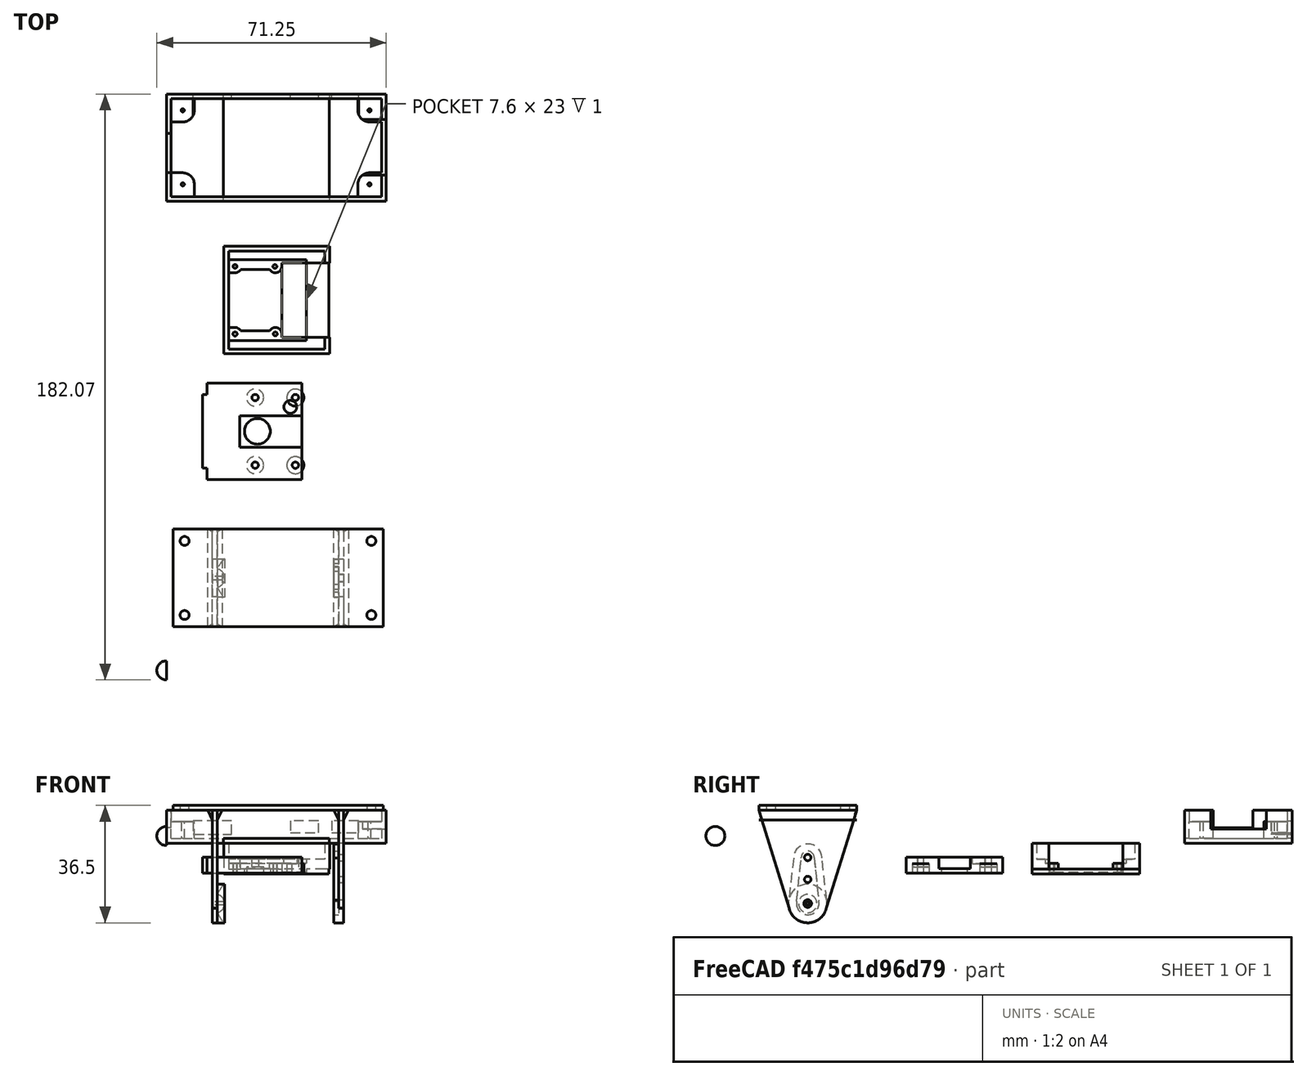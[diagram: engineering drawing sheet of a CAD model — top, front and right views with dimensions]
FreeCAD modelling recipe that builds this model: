
FCSTD DOCUMENT  (FreeCAD 0.18.3R)
Label: Vertical.Turning.PI.Box
License: All rights reserved
LicenseURL: http://en.wikipedia.org/wiki/All_rights_reserved
objects: Part::Part2DObjectPython×108, Part::Extrusion×94, Part::Cut×46, Part::MultiFuse×22, Part::FeaturePython×6, Part::Sphere×2, App::DocumentObjectGroup×2
note: 278 computed .brp shape members not serialized (recipe doc carries the construction recipe); baked Part::Feature solids carry a one-line shape summary decoded from their .brp

FEATURE [Part::Part2DObjectPython] Rectangle  # Draft 2D object (typed FeaturePython)
  ChamferSize = 0
  Columns = 1
  FilletRadius = 0
  Height = 33.4
  Length = 68.3
  MakeFace = true
  Placement = pos=(0,0,0) rot=(1,0,0;3.14159rad)
  Rows = 1
FEATURE [Part::Part2DObjectPython] Rectangle001  # Draft 2D object (typed FeaturePython)
  ChamferSize = 0
  Columns = 1
  FilletRadius = 0
  Height = 30.4
  Length = 65.3
  MakeFace = true
  Placement = pos=(1.5,-1.5,0) rot=(1,0,0;3.14159rad)
  Rows = 1
FEATURE [Part::Part2DObjectPython] Circle004  # Draft 2D object (typed FeaturePython)
  FirstAngle = 0
  LastAngle = 0
  MakeFace = true
  Placement = pos=(5.1,-5.1,-8.3) rot=(0,0,-1;1.5708rad)
  Radius = 3.6
FEATURE [Part::Part2DObjectPython] Circle006  # Draft 2D object (typed FeaturePython)
  FirstAngle = 0
  LastAngle = 0
  MakeFace = true
  Placement = pos=(63.1,-5.1,-8.3) rot=(0,0,1;0rad)
  Radius = 3.6
FEATURE [Part::Part2DObjectPython] Rectangle006  # Draft 2D object (typed FeaturePython)
  ChamferSize = 0
  Columns = 1
  FilletRadius = 0
  Height = 4.1
  Length = 11.9
  MakeFace = true
  Placement = pos=(8.375,-1.5,-7) rot=(1,0,0;1.5708rad)
  Rows = 1
FEATURE [Part::Part2DObjectPython] Rectangle007  # Draft 2D object (typed FeaturePython)
  ChamferSize = 0
  Columns = 1
  FilletRadius = 0
  Height = 3.7
  Length = 8.7
  MakeFace = true
  Placement = pos=(38.55,-1.5,-6.5) rot=(1,0,0;1.5708rad)
  Rows = 1
FEATURE [Part::Part2DObjectPython] Rectangle008  # Draft 2D object (typed FeaturePython)
  ChamferSize = 0
  Columns = 1
  FilletRadius = 0
  Height = 3.7
  Length = 8.4
  MakeFace = true
  Placement = pos=(51.35,-1.5,-6.5) rot=(1,0,0;1.5708rad)
  Rows = 1
  Support = -> [Rectangle007]
FEATURE [Part::Extrusion] Extrude020
  Base = -> Circle006
  Dir = (0,0,1)
  DirMode = 2
  FaceMakerClass = Part::FaceMakerBullseye
  LengthFwd = 5.3
  LengthRev = 0
  Solid = false
  Symmetric = false
FEATURE [Part::Extrusion] Extrude021
  Base = -> Circle004
  Dir = (0,0,1)
  DirMode = 2
  FaceMakerClass = Part::FaceMakerBullseye
  LengthFwd = 5.3
  LengthRev = 0
  Solid = false
  Symmetric = false
FEATURE [Part::Part2DObjectPython] Rectangle013  # Draft 2D object (typed FeaturePython)
  ChamferSize = 0
  Columns = 1
  FilletRadius = 0
  Height = 7.2
  Length = 3.6
  MakeFace = true
  Placement = pos=(1.5,-8.7,-8.3) rot=(0,0,1;0rad)
  Rows = 1
  Support = -> [Rectangle]
FEATURE [Part::Part2DObjectPython] Rectangle014  # Draft 2D object (typed FeaturePython)
  ChamferSize = 0
  Columns = 1
  FilletRadius = 0
  Height = 3.6
  Length = 7.2
  MakeFace = true
  Placement = pos=(1.5,-5.1,-8.3) rot=(0,0,1;0rad)
  Rows = 1
FEATURE [Part::Part2DObjectPython] Circle008  # Draft 2D object (typed FeaturePython)
  FirstAngle = 0
  LastAngle = 0
  MakeFace = true
  Placement = pos=(63.1,-5.1,-8.3) rot=(0,0,1;0rad)
  Radius = 0.5
FEATURE [Part::Extrusion] Extrude027
  Base = -> Circle008
  Dir = (0,0,1)
  DirMode = 2
  FaceMakerClass = Part::FaceMakerBullseye
  LengthFwd = 5.3
  LengthRev = 0
  Solid = false
  Symmetric = false
FEATURE [Part::Extrusion] Extrude028
  Base = -> Rectangle013
  Dir = (0,0,1)
  DirMode = 2
  FaceMakerClass = Part::FaceMakerBullseye
  LengthFwd = 5.3
  LengthRev = 0
  Solid = false
  Symmetric = false
FEATURE [Part::Extrusion] Extrude029
  Base = -> Rectangle014
  Dir = (0,0,1)
  DirMode = 2
  FaceMakerClass = Part::FaceMakerBullseye
  LengthFwd = 5.3
  LengthRev = 0
  Solid = false
  Symmetric = false
FEATURE [Part::MultiFuse] Fusion002
  Shapes = -> [Extrude028,Extrude029,Extrude021]
FEATURE [Part::Part2DObjectPython] Circle009  # Draft 2D object (typed FeaturePython)
  FirstAngle = 0
  LastAngle = 0
  MakeFace = true
  Placement = pos=(5.1,-5.1,-8.3) rot=(0,0,1;0rad)
  Radius = 0.5
FEATURE [Part::Extrusion] Extrude030
  Base = -> Circle009
  Dir = (0,0,1)
  DirMode = 2
  FaceMakerClass = Part::FaceMakerBullseye
  LengthFwd = 5.3
  LengthRev = 0
  Solid = false
  Symmetric = false
FEATURE [Part::Cut] Cut002
  Base = -> Fusion002
  Tool = -> Extrude030
FEATURE [Part::Part2DObjectPython] Circle010  # Draft 2D object (typed FeaturePython)
  FirstAngle = 0
  LastAngle = 0
  MakeFace = true
  Placement = pos=(5.1,-28.1,-8.3) rot=(1,0,0;3.14159rad)
  Radius = 0.5
FEATURE [Part::Extrusion] Extrude033
  Base = -> Circle010
  Dir = (0,0,-1)
  DirMode = 2
  FaceMakerClass = Part::FaceMakerBullseye
  LengthFwd = -5.3
  LengthRev = 0
  Solid = false
  Symmetric = false
FEATURE [Part::Part2DObjectPython] Circle011  # Draft 2D object (typed FeaturePython)
  FirstAngle = 0
  LastAngle = 0
  MakeFace = true
  Placement = pos=(5.1,-28.1,-8.3) rot=(1,0,0;3.14159rad)
  Radius = 3.6
FEATURE [Part::Part2DObjectPython] Rectangle019  # Draft 2D object (typed FeaturePython)
  ChamferSize = 0
  Columns = 1
  FilletRadius = 0
  Height = 3.8
  Length = 7.2
  MakeFace = true
  Placement = pos=(1.5,-31.9,-8.3) rot=(0,0,1;0rad)
  Rows = 1
FEATURE [Part::Part2DObjectPython] Rectangle020  # Draft 2D object (typed FeaturePython)
  ChamferSize = 0
  Columns = 1
  FilletRadius = 0
  Height = 7.4
  Length = 3.6
  MakeFace = true
  Placement = pos=(1.5,-31.9,-8.3) rot=(0,0,1;0rad)
  Rows = 1
FEATURE [Part::Extrusion] Extrude
  Base = -> Circle011
  Dir = (0,0,-1)
  DirMode = 2
  FaceMakerClass = Part::FaceMakerBullseye
  LengthFwd = -5.3
  LengthRev = 0
  Solid = false
  Symmetric = false
FEATURE [Part::Extrusion] Extrude034
  Base = -> Rectangle019
  Dir = (0,0,1)
  DirMode = 2
  FaceMakerClass = Part::FaceMakerBullseye
  LengthFwd = 5.3
  LengthRev = 0
  Solid = false
  Symmetric = false
FEATURE [Part::Extrusion] Extrude035
  Base = -> Rectangle020
  Dir = (0,0,1)
  DirMode = 2
  FaceMakerClass = Part::FaceMakerBullseye
  LengthFwd = 5.3
  LengthRev = 0
  Solid = false
  Symmetric = false
FEATURE [Part::MultiFuse] Fusion003
  Shapes = -> [Extrude034,Extrude035,Extrude]
FEATURE [Part::Cut] Cut003
  Base = -> Fusion003
  Tool = -> Extrude033
FEATURE [Part::Extrusion] Extrude036
  Base = -> Rectangle001
  Dir = (0,0,-1)
  DirMode = 2
  FaceMakerClass = Part::FaceMakerBullseye
  LengthFwd = 8.3
  LengthRev = 0
  Solid = false
  Symmetric = false
FEATURE [Part::Extrusion] Extrude037
  Base = -> Rectangle
  Dir = (0,0,-1)
  DirMode = 2
  FaceMakerClass = Part::FaceMakerBullseye
  LengthFwd = 9.8
  LengthRev = 0
  Solid = false
  Symmetric = false
FEATURE [Part::Part2DObjectPython] Circle012  # Draft 2D object (typed FeaturePython)
  FirstAngle = 0
  LastAngle = 0
  MakeFace = true
  Placement = pos=(63.1,-28.1,-3) rot=(0,0,1;0rad)
  Radius = 3.6
FEATURE [Part::Part2DObjectPython] Circle013  # Draft 2D object (typed FeaturePython)
  FirstAngle = 0
  LastAngle = 0
  MakeFace = true
  Placement = pos=(63.1,-28.1,-3) rot=(0,0,1;0rad)
  Radius = 0.5
FEATURE [Part::Part2DObjectPython] Rectangle021  # Draft 2D object (typed FeaturePython)
  ChamferSize = 0
  Columns = 1
  FilletRadius = 0
  Height = 7.4
  Length = 3.7
  MakeFace = true
  Placement = pos=(63.1,-31.9,-3) rot=(0,0,1;0rad)
  Rows = 1
FEATURE [Part::Part2DObjectPython] Rectangle022  # Draft 2D object (typed FeaturePython)
  ChamferSize = 0
  Columns = 1
  FilletRadius = 0
  Height = 3.8
  Length = 7.3
  MakeFace = true
  Placement = pos=(59.5,-31.9,-3) rot=(0,0,1;0rad)
  Rows = 1
FEATURE [Part::Extrusion] Extrude038
  Base = -> Rectangle021
  Dir = (0,0,1)
  DirMode = 2
  FaceMakerClass = Part::FaceMakerBullseye
  LengthFwd = -5.3
  LengthRev = 0
  Solid = false
  Symmetric = false
FEATURE [Part::Extrusion] Extrude039
  Base = -> Rectangle022
  Dir = (0,0,1)
  DirMode = 2
  FaceMakerClass = Part::FaceMakerBullseye
  LengthFwd = -5.3
  LengthRev = 0
  Solid = false
  Symmetric = false
FEATURE [Part::Extrusion] Extrude040
  Base = -> Circle012
  Dir = (0,0,1)
  DirMode = 2
  FaceMakerClass = Part::FaceMakerBullseye
  LengthFwd = -5.3
  LengthRev = 0
  Solid = false
  Symmetric = false
FEATURE [Part::Extrusion] Extrude041
  Base = -> Circle013
  Dir = (0,0,1)
  DirMode = 2
  FaceMakerClass = Part::FaceMakerBullseye
  LengthFwd = -5.3
  LengthRev = 0
  Solid = false
  Symmetric = false
FEATURE [Part::MultiFuse] Fusion
  Shapes = -> [Extrude038,Extrude039,Extrude040]
FEATURE [Part::Cut] Cut
  Base = -> Fusion
  Tool = -> Extrude041
FEATURE [Part::Part2DObjectPython] Rectangle024  # Draft 2D object (typed FeaturePython)
  ChamferSize = 0
  Columns = 1
  FilletRadius = 0
  Height = 3.6
  Length = 7.3
  MakeFace = true
  Placement = pos=(59.5,-5.1,-3) rot=(0,0,1;0rad)
  Rows = 1
FEATURE [Part::Part2DObjectPython] Rectangle025  # Draft 2D object (typed FeaturePython)
  ChamferSize = 0
  Columns = 1
  FilletRadius = 0
  Height = 7.19976
  Length = 3.7019
  MakeFace = true
  Placement = pos=(63.1,-8.7,-3) rot=(0,0,1;0rad)
  Rows = 1
FEATURE [Part::Extrusion] Extrude042
  Base = -> Rectangle025
  Dir = (0,0,1)
  DirMode = 2
  FaceMakerClass = Part::FaceMakerBullseye
  LengthFwd = -5.3
  LengthRev = 0
  Solid = false
  Symmetric = false
FEATURE [Part::Extrusion] Extrude043
  Base = -> Rectangle024
  Dir = (0,0,1)
  DirMode = 2
  FaceMakerClass = Part::FaceMakerBullseye
  LengthFwd = -5.3
  LengthRev = 0
  Solid = false
  Symmetric = false
FEATURE [Part::MultiFuse] Fusion004
  Shapes = -> [Extrude043,Extrude042,Extrude020]
FEATURE [Part::Cut] Cut005
  Base = -> Fusion004
  Tool = -> Extrude027
FEATURE [Part::Extrusion] Extrude046
  Base = -> Rectangle006
  Dir = (0,-1,2e-16)
  DirMode = 2
  FaceMakerClass = Part::FaceMakerBullseye
  LengthFwd = 7
  LengthRev = 0
  Solid = false
  Symmetric = false
FEATURE [Part::Cut] Cut008
  Base = -> Cut002
  Tool = -> Extrude046
FEATURE [Part::Part2DObjectPython] Rectangle028  # Draft 2D object (typed FeaturePython)
  ChamferSize = 0
  Columns = 1
  FilletRadius = 0
  Height = 4.2
  Length = 11.9
  MakeFace = true
  Placement = pos=(8.375,-1.5,-7) rot=(1,0,0;1.5708rad)
  Rows = 1
FEATURE [Part::Part2DObjectPython] Rectangle029  # Draft 2D object (typed FeaturePython)
  ChamferSize = 0
  Columns = 1
  FilletRadius = 0
  Height = 3.6
  Length = 8.4
  MakeFace = true
  Placement = pos=(51.35,-1.5,-6.5) rot=(1,0,0;1.5708rad)
  Rows = 1
FEATURE [Part::Extrusion] Extrude050
  Base = -> Rectangle029
  Dir = (0,-1,2e-16)
  DirMode = 2
  FaceMakerClass = Part::FaceMakerBullseye
  LengthFwd = 7
  LengthRev = 0
  Placement = pos=(7.1e-15,-9e-16,0) rot=(0,0,1;0rad)
  Solid = false
  Symmetric = false
FEATURE [Part::Part2DObjectPython] Circle018  # Draft 2D object (typed FeaturePython)
  FirstAngle = 0
  LastAngle = 0
  MakeFace = true
  Placement = pos=(80.1343,-53.566,-3.6) rot=(0,0,1;0rad)
  Radius = 2
FEATURE [Part::Part2DObjectPython] Circle019  # Draft 2D object (typed FeaturePython)
  FirstAngle = 0
  LastAngle = 0
  MakeFace = true
  Placement = pos=(80.1343,-74.566,-3.6) rot=(0,0,1;0rad)
  Radius = 2
FEATURE [Part::Part2DObjectPython] Circle020  # Draft 2D object (typed FeaturePython)
  FirstAngle = 0
  LastAngle = 0
  MakeFace = true
  Placement = pos=(67.6343,-74.566,-3.6) rot=(0,0,1;0rad)
  Radius = 2
FEATURE [Part::Part2DObjectPython] Circle021  # Draft 2D object (typed FeaturePython)
  FirstAngle = 0
  LastAngle = 0
  MakeFace = true
  Placement = pos=(67.6343,-53.566,-3.6) rot=(0,0,1;0rad)
  Radius = 2
FEATURE [Part::Part2DObjectPython] Rectangle043  # Draft 2D object (typed FeaturePython)
  ChamferSize = 0
  Columns = 1
  FilletRadius = 0
  Height = 30
  Length = 29.4
  MakeFace = true
  Placement = pos=(12.6799,-119.849,-14.1) rot=(0,0,1;0rad)
  Rows = 1
FEATURE [Part::Part2DObjectPython] Rectangle044  # Draft 2D object (typed FeaturePython)
  ChamferSize = 0
  Columns = 1
  FilletRadius = 0
  Height = 22.8
  Length = 1.5
  MakeFace = true
  Placement = pos=(11.1799,-116.249,-14.1) rot=(0,0,1;0rad)
  Rows = 1
FEATURE [Part::Part2DObjectPython] Rectangle045  # Draft 2D object (typed FeaturePython)
  ChamferSize = 0
  Columns = 1
  FilletRadius = 0
  Height = 9.8
  Length = 19.3
  MakeFace = true
  Placement = pos=(22.7799,-109.749,-14.1) rot=(0,0,1;0rad)
  Rows = 1
FEATURE [Part::Part2DObjectPython] Circle022  # Draft 2D object (typed FeaturePython)
  FirstAngle = 0
  LastAngle = 0
  MakeFace = true
  Placement = pos=(28.2799,-104.849,-14.1) rot=(0,0,1;0rad)
  Radius = 4
FEATURE [Part::MultiFuse] Fusion013
  Shapes = -> [Cut005,Cut]
FEATURE [Part::Part2DObjectPython] Circle  # Draft 2D object (typed FeaturePython)
  FirstAngle = 0
  LastAngle = 0
  MakeFace = true
  Placement = pos=(27.5799,-94.3491,-14.1) rot=(0,0,1;0rad)
  Radius = 1
FEATURE [Part::Part2DObjectPython] Circle023  # Draft 2D object (typed FeaturePython)
  FirstAngle = 0
  LastAngle = 0
  MakeFace = true
  Placement = pos=(40.0799,-94.3491,-14.1) rot=(0,0,1;0rad)
  Radius = 1
FEATURE [Part::Part2DObjectPython] Circle024  # Draft 2D object (typed FeaturePython)
  FirstAngle = 0
  LastAngle = 0
  MakeFace = true
  Placement = pos=(40.0799,-115.349,-14.1) rot=(0,0,1;0rad)
  Radius = 1
FEATURE [Part::Part2DObjectPython] Circle025  # Draft 2D object (typed FeaturePython)
  FirstAngle = 0
  LastAngle = 0
  MakeFace = true
  Placement = pos=(27.5799,-115.349,-14.1) rot=(0,0,1;0rad)
  Radius = 1
FEATURE [Part::Extrusion] Extrude083
  Base = -> Rectangle043
  Dir = (0,0,1)
  DirMode = 2
  FaceMakerClass = Part::FaceMakerBullseye
  LengthFwd = -5
  LengthRev = 0
  Solid = false
  Symmetric = false
FEATURE [Part::Extrusion] Extrude085
  Base = -> Rectangle045
  Dir = (0,0,1)
  DirMode = 2
  FaceMakerClass = Part::FaceMakerBullseye
  LengthFwd = -3.5
  LengthRev = 0
  Solid = false
  Symmetric = false
FEATURE [Part::Extrusion] Extrude086
  Base = -> Circle
  Dir = (0,0,1)
  DirMode = 2
  FaceMakerClass = Part::FaceMakerBullseye
  LengthFwd = -5
  LengthRev = 0
  Solid = false
  Symmetric = false
FEATURE [Part::Extrusion] Extrude087
  Base = -> Circle023
  Dir = (0,0,1)
  DirMode = 2
  FaceMakerClass = Part::FaceMakerBullseye
  LengthFwd = -5
  LengthRev = 0
  Solid = false
  Symmetric = false
FEATURE [Part::Extrusion] Extrude088
  Base = -> Circle025
  Dir = (0,0,1)
  DirMode = 2
  FaceMakerClass = Part::FaceMakerBullseye
  LengthFwd = -5
  LengthRev = 0
  Solid = false
  Symmetric = false
FEATURE [Part::Extrusion] Extrude089
  Base = -> Circle024
  Dir = (0,0,1)
  DirMode = 2
  FaceMakerClass = Part::FaceMakerBullseye
  LengthFwd = -5
  LengthRev = 0
  Solid = false
  Symmetric = false
FEATURE [Part::Cut] Cut027
  Base = -> Extrude083
  Tool = -> Extrude085
FEATURE [Part::Extrusion] Extrude095
  Base = -> Rectangle044
  Dir = (0,0,1)
  DirMode = 2
  FaceMakerClass = Part::FaceMakerBullseye
  LengthFwd = -5
  LengthRev = 0
  Solid = false
  Symmetric = false
FEATURE [Part::Part2DObjectPython] Rectangle048  # Draft 2D object (typed FeaturePython)
  ChamferSize = 0
  Columns = 1
  FilletRadius = 0
  Height = 4.99807
  Length = 12.3
  MakeFace = true
  Placement = pos=(1.5,-24.5,-4.99807) rot=(0.57735,0.57735,0.57735;2.0944rad)
  Rows = 1
FEATURE [Part::Extrusion] Extrude096
  Base = -> Rectangle048
  Dir = (1,0,0)
  DirMode = 2
  FaceMakerClass = Part::FaceMakerBullseye
  LengthFwd = -1.5
  LengthRev = 0
  Solid = false
  Symmetric = false
FEATURE [Part::Part2DObjectPython] Circle030  # Draft 2D object (typed FeaturePython)
  FirstAngle = 0
  LastAngle = 0
  MakeFace = true
  Placement = pos=(27.5799,-94.3491,-19.1) rot=(0,0,1;0rad)
  Radius = 2.65
FEATURE [Part::Part2DObjectPython] Circle031  # Draft 2D object (typed FeaturePython)
  FirstAngle = 0
  LastAngle = 0
  MakeFace = true
  Placement = pos=(27.5799,-115.349,-19.1) rot=(0,0,1;0rad)
  Radius = 2.65
FEATURE [Part::Part2DObjectPython] Circle032  # Draft 2D object (typed FeaturePython)
  FirstAngle = 0
  LastAngle = 0
  MakeFace = true
  Placement = pos=(40.0799,-115.349,-19.1) rot=(0,0,1;0rad)
  Radius = 2.65
FEATURE [Part::Part2DObjectPython] Circle033  # Draft 2D object (typed FeaturePython)
  FirstAngle = 0
  LastAngle = 0
  MakeFace = true
  Placement = pos=(40.0799,-94.3491,-19.1) rot=(0,0,1;0rad)
  Radius = 2.65
FEATURE [Part::Extrusion] Extrude104
  Base = -> Circle032
  Dir = (0,0,1)
  DirMode = 2
  FaceMakerClass = Part::FaceMakerBullseye
  LengthFwd = 3
  LengthRev = 0
  Solid = false
  Symmetric = false
FEATURE [Part::Extrusion] Extrude105
  Base = -> Circle033
  Dir = (0,0,1)
  DirMode = 2
  FaceMakerClass = Part::FaceMakerBullseye
  LengthFwd = 3
  LengthRev = 0
  Solid = false
  Symmetric = false
FEATURE [Part::Part2DObjectPython] Rectangle049  # Draft 2D object (typed FeaturePython)
  ChamferSize = 0
  Columns = 1
  FilletRadius = 0
  Height = 33.4
  Length = 32.95
  MakeFace = true
  Placement = pos=(17.675,-33.4,-10.8) rot=(0,0,1;0rad)
  Rows = 1
FEATURE [Part::Part2DObjectPython] Rectangle060  # Draft 2D object (typed FeaturePython)
  ChamferSize = 0
  Columns = 1
  FilletRadius = 0
  Height = 23
  Length = 14.4
  MakeFace = true
  Placement = pos=(52.2343,-52.566,-9.8) rot=(1,0,0;3.14159rad)
  Rows = 1
FEATURE [Part::Part2DObjectPython] Rectangle053  # Draft 2D object (typed FeaturePython)
  ChamferSize = 0
  Columns = 1
  FilletRadius = 0
  Height = 33.4
  Length = 32.9
  MakeFace = true
  Placement = pos=(50.7343,-47.366,-9.8) rot=(1,0,0;3.14159rad)
  Rows = 1
FEATURE [Part::Part2DObjectPython] Rectangle061  # Draft 2D object (typed FeaturePython)
  ChamferSize = 0
  Columns = 1
  FilletRadius = 0
  Height = 25.1
  Length = 24.1
  MakeFace = true
  Placement = pos=(58.0343,-51.516,-9.8) rot=(1,0,0;3.14159rad)
  Rows = 1
FEATURE [Part::Part2DObjectPython] Rectangle059  # Draft 2D object (typed FeaturePython)
  ChamferSize = 0
  Columns = 1
  FilletRadius = 0
  Height = 19
  Length = 15.5
  MakeFace = true
  Placement = pos=(66.6343,-54.566,-9.8) rot=(1,0,0;3.14159rad)
  Rows = 1
FEATURE [Part::Part2DObjectPython] Rectangle062  # Draft 2D object (typed FeaturePython)
  ChamferSize = 0
  Columns = 1
  FilletRadius = 0
  Height = 30.4
  Length = 29.9
  MakeFace = true
  Placement = pos=(52.2343,-48.866,-9.8) rot=(1,0,0;3.14159rad)
  Rows = 1
FEATURE [Part::Extrusion] Extrude107
  Base = -> Rectangle053
  Dir = (0,0,-1)
  DirMode = 2
  FaceMakerClass = Part::FaceMakerBullseye
  LengthFwd = -9
  LengthRev = 0
  Solid = false
  Symmetric = false
FEATURE [Part::Extrusion] Extrude116
  Base = -> Rectangle062
  Dir = (0,0,-1)
  DirMode = 2
  FaceMakerClass = Part::FaceMakerBullseye
  LengthFwd = -5
  LengthRev = 0
  Solid = false
  Symmetric = false
FEATURE [Part::Cut] Cut046
  Base = -> Extrude107
  Tool = -> Extrude116
FEATURE [Part::Extrusion] Extrude117
  Base = -> Rectangle061
  Dir = (0,0,-1)
  DirMode = 2
  FaceMakerClass = Part::FaceMakerBullseye
  LengthFwd = -6.2
  LengthRev = 0
  Solid = false
  Symmetric = false
FEATURE [Part::Part2DObjectPython] Rectangle063  # Draft 2D object (typed FeaturePython)
  ChamferSize = 0
  Columns = 1
  FilletRadius = 0
  Height = 23
  Length = 1.5
  MakeFace = true
  Placement = pos=(50.7343,-75.566,-9.8) rot=(0,0,1;0rad)
  Rows = 1
FEATURE [Part::Extrusion] Extrude128
  Base = -> Rectangle063
  Dir = (0,0,1)
  DirMode = 2
  FaceMakerClass = Part::FaceMakerBullseye
  LengthFwd = 8
  LengthRev = 0
  Solid = false
  Symmetric = false
FEATURE [Part::Part2DObjectPython] Rectangle064  # Draft 2D object (typed FeaturePython)
  ChamferSize = 0
  Columns = 1
  FilletRadius = 0
  Height = 1
  Length = 2
  MakeFace = true
  Placement = pos=(80.1343,-73.566,-3.6) rot=(0,0,1;0rad)
  Rows = 1
FEATURE [Part::Part2DObjectPython] Rectangle065  # Draft 2D object (typed FeaturePython)
  ChamferSize = 0
  Columns = 1
  FilletRadius = 0
  Height = 1
  Length = 2
  MakeFace = true
  Placement = pos=(80.1343,-55.566,-3.6) rot=(0,0,1;0rad)
  Rows = 1
FEATURE [Part::Part2DObjectPython] Rectangle066  # Draft 2D object (typed FeaturePython)
  ChamferSize = 0
  Columns = 1
  FilletRadius = 0
  Height = 1
  Length = 1
  MakeFace = true
  Placement = pos=(65.6343,-75.566,-3.6) rot=(0,0,1;0rad)
  Rows = 1
FEATURE [Part::Part2DObjectPython] Rectangle067  # Draft 2D object (typed FeaturePython)
  ChamferSize = 0
  Columns = 1
  FilletRadius = 0
  Height = 1
  Length = 1
  MakeFace = true
  Placement = pos=(65.6343,-53.566,-3.6) rot=(0,0,1;0rad)
  Rows = 1
FEATURE [Part::Part2DObjectPython] Wire002  # Draft 2D object (typed FeaturePython)
  ChamferSize = 0
  Closed = true
  End = (50.625,-33.4,-10.8)
  FilletRadius = 0
  Length = 3.5
  MakeFace = true
  Placement = pos=(50.625,-33.4,-9.8) rot=(1,0,0;1.5708rad)
  Points = (3) [(0,0,0),(1.05,0,0),(0,-1,0)]
  Start = (50.625,-33.4,-9.8)
  Subdivisions = 0
FEATURE [Part::Part2DObjectPython] Wire003  # Draft 2D object (typed FeaturePython)
  ChamferSize = 0
  Closed = true
  End = (17.675,-33.4,-9.8)
  FilletRadius = 0
  Length = 3.5
  MakeFace = true
  Placement = pos=(16.625,-33.4,-9.8) rot=(1,0,0;1.5708rad)
  Points = (3) [(0,0,0),(1.05,-1,0),(1.05,0,0)]
  Start = (16.625,-33.4,-9.8)
  Subdivisions = 0
FEATURE [Part::Extrusion] Extrude140
  Base = -> Rectangle059
  Dir = (0,0,-1)
  DirMode = 2
  FaceMakerClass = Part::FaceMakerBullseye
  LengthFwd = -8
  LengthRev = 0
  Solid = false
  Symmetric = false
FEATURE [Part::Extrusion] Extrude141
  Base = -> Rectangle060
  Dir = (0,0,-1)
  DirMode = 2
  FaceMakerClass = Part::FaceMakerBullseye
  LengthFwd = -8
  LengthRev = 0
  Solid = false
  Symmetric = false
FEATURE [Part::Extrusion] Extrude149
  Base = -> Circle020
  Dir = (0,0,1)
  DirMode = 2
  FaceMakerClass = Part::FaceMakerBullseye
  LengthFwd = 2.1
  LengthRev = 0
  Solid = false
  Symmetric = false
FEATURE [Part::Extrusion] Extrude150
  Base = -> Rectangle066
  Dir = (0,0,1)
  DirMode = 2
  FaceMakerClass = Part::FaceMakerBullseye
  LengthFwd = 2.1
  LengthRev = 0
  Solid = false
  Symmetric = false
FEATURE [Part::Extrusion] Extrude152
  Base = -> Circle019
  Dir = (0,0,1)
  DirMode = 2
  FaceMakerClass = Part::FaceMakerBullseye
  LengthFwd = 2.1
  LengthRev = 0
  Solid = false
  Symmetric = false
FEATURE [Part::Extrusion] Extrude153
  Base = -> Rectangle064
  Dir = (0,0,1)
  DirMode = 2
  FaceMakerClass = Part::FaceMakerBullseye
  LengthFwd = 2.1
  LengthRev = 0
  Solid = false
  Symmetric = false
FEATURE [Part::Extrusion] Extrude155
  Base = -> Circle018
  Dir = (0,0,1)
  DirMode = 2
  FaceMakerClass = Part::FaceMakerBullseye
  LengthFwd = 2.1
  LengthRev = 0
  Solid = false
  Symmetric = false
FEATURE [Part::Extrusion] Extrude156
  Base = -> Rectangle065
  Dir = (0,0,1)
  DirMode = 2
  FaceMakerClass = Part::FaceMakerBullseye
  LengthFwd = 2.1
  LengthRev = 0
  Solid = false
  Symmetric = false
FEATURE [Part::Extrusion] Extrude158
  Base = -> Circle021
  Dir = (0,0,1)
  DirMode = 2
  FaceMakerClass = Part::FaceMakerBullseye
  LengthFwd = 2.1
  LengthRev = 0
  Solid = false
  Symmetric = false
FEATURE [Part::Extrusion] Extrude159
  Base = -> Rectangle067
  Dir = (0,0,1)
  DirMode = 2
  FaceMakerClass = Part::FaceMakerBullseye
  LengthFwd = 2.1
  LengthRev = 0
  Solid = false
  Symmetric = false
FEATURE [Part::MultiFuse] Fusion024
  Shapes = -> [Extrude149,Extrude150]
FEATURE [Part::MultiFuse] Fusion025
  Shapes = -> [Extrude158,Extrude159]
FEATURE [Part::Extrusion] Extrude160
  Base = -> Circle022
  Dir = (0,0,1)
  DirMode = 2
  FaceMakerClass = Part::FaceMakerBullseye
  LengthFwd = -5
  LengthRev = 0
  Solid = false
  Symmetric = false
FEATURE [Part::Part2DObjectPython] Circle034  # Draft 2D object (typed FeaturePython)
  FirstAngle = 0
  LastAngle = 0
  MakeFace = true
  Placement = pos=(38.5147,-97.236,-14.1) rot=(0,0,1;0rad)
  Radius = 2
FEATURE [Part::Part2DObjectPython] Rectangle070  # Draft 2D object (typed FeaturePython)
  ChamferSize = 0
  Columns = 1
  FilletRadius = 0
  Height = 23
  Length = 7.6
  MakeFace = true
  Placement = pos=(58.0343,-75.566,-3.6) rot=(0,0,1;0rad)
  Rows = 1
FEATURE [Part::Extrusion] Extrude162
  Base = -> Rectangle070
  Dir = (0,0,1)
  DirMode = 2
  FaceMakerClass = Part::FaceMakerBullseye
  LengthFwd = 2.8
  LengthRev = 0
  Solid = false
  Symmetric = false
FEATURE [Part::Part2DObjectPython] Circle036  # Draft 2D object (typed FeaturePython)
  FirstAngle = 0
  LastAngle = 0
  MakeFace = true
  Placement = pos=(80.1343,-53.566,-3.6) rot=(0,0,1;0rad)
  Radius = 0.6
FEATURE [Part::MultiFuse] Fusion026
  Shapes = -> [Extrude156,Extrude155]
FEATURE [Part::Extrusion] Extrude163
  Base = -> Circle036
  Dir = (0,0,1)
  DirMode = 2
  FaceMakerClass = Part::FaceMakerBullseye
  LengthFwd = 2.8
  LengthRev = 0
  Solid = false
  Symmetric = false
FEATURE [Part::Part2DObjectPython] Circle037  # Draft 2D object (typed FeaturePython)
  FirstAngle = 0
  LastAngle = 0
  MakeFace = true
  Placement = pos=(67.7487,-53.6033,-3.6) rot=(1,0,0;3.14159rad)
  Radius = 0.6
FEATURE [Part::Part2DObjectPython] Circle038  # Draft 2D object (typed FeaturePython)
  FirstAngle = 0
  LastAngle = 0
  MakeFace = true
  Placement = pos=(67.6343,-74.566,-3.6) rot=(0,0,1;0rad)
  Radius = 0.6
FEATURE [Part::Extrusion] Extrude165
  Base = -> Circle038
  Dir = (0,0,1)
  DirMode = 2
  FaceMakerClass = Part::FaceMakerBullseye
  LengthFwd = 2.8
  LengthRev = 0
  Solid = false
  Symmetric = false
FEATURE [Part::Extrusion] Extrude166
  Base = -> Circle037
  Dir = (0,0,-1)
  DirMode = 2
  FaceMakerClass = Part::FaceMakerBullseye
  LengthFwd = -2.8
  LengthRev = 0
  Solid = false
  Symmetric = false
FEATURE [Part::MultiFuse] Fusion032
  Shapes = -> [Extrude152,Extrude153]
FEATURE [Part::Part2DObjectPython] Rectangle071  # Draft 2D object (typed FeaturePython)
  ChamferSize = 0
  Columns = 1
  FilletRadius = 0
  Height = 33.4
  Length = 32.95
  MakeFace = true
  Placement = pos=(17.675,2e-15,-9.8) rot=(1,0,0;3.14159rad)
  Rows = 1
FEATURE [Part::Extrusion] Extrude168
  Base = -> Rectangle071
  Dir = (0,0,-1)
  DirMode = 2
  FaceMakerClass = Part::FaceMakerBullseye
  LengthFwd = -1.5
  LengthRev = 0
  Solid = false
  Symmetric = false
FEATURE [Part::Cut] Cut004
  Base = -> Extrude037
  Tool = -> Extrude036
FEATURE [Part::Part2DObjectPython] Rectangle027  # Draft 2D object (typed FeaturePython)
  ChamferSize = 0
  Columns = 1
  FilletRadius = 0
  Height = 5.4
  Length = 17.3
  MakeFace = true
  Placement = pos=(60.9006,-7.95,-5.4) rot=(0.57735,-0.57735,-0.57735;2.0944rad)
  Rows = 1
  Support = -> [Cut004]
FEATURE [Part::Extrusion] Extrude081
  Base = -> Rectangle027
  Dir = (-1,0,0)
  DirMode = 2
  FaceMakerClass = Part::FaceMakerBullseye
  LengthFwd = -8
  LengthRev = 0
  Solid = false
  Symmetric = false
FEATURE [Part::Extrusion] Extrude169
  Base = -> Rectangle028
  Dir = (0,-1,2e-16)
  DirMode = 2
  FaceMakerClass = Part::FaceMakerBullseye
  LengthFwd = -1.5
  LengthRev = 0
  Solid = false
  Symmetric = false
FEATURE [Part::Extrusion] Extrude170
  Base = -> Rectangle007
  Dir = (0,-1,2e-16)
  DirMode = 2
  FaceMakerClass = Part::FaceMakerBullseye
  LengthFwd = -1.5
  LengthRev = 0
  Solid = false
  Symmetric = false
FEATURE [Part::Extrusion] Extrude171
  Base = -> Rectangle008
  Dir = (0,-1,2e-16)
  DirMode = 2
  FaceMakerClass = Part::FaceMakerBullseye
  LengthFwd = -1.5
  LengthRev = 0
  Solid = false
  Symmetric = false
FEATURE [Part::MultiFuse] Fusion034
  Shapes = -> [Cut003,Cut008,Fusion013,Cut004]
FEATURE [Part::Cut] Cut079
  Base = -> Fusion034
  Tool = -> Extrude081
FEATURE [Part::Cut] Cut080
  Base = -> Cut079
  Tool = -> Extrude096
FEATURE [Part::Cut] Cut081
  Base = -> Cut080
  Tool = -> Extrude169
FEATURE [Part::Cut] Cut082
  Base = -> Cut081
  Tool = -> Extrude170
FEATURE [Part::Cut] Cut083
  Base = -> Cut082
  Tool = -> Extrude171
FEATURE [Part::Cut] Cut084
  Base = -> Cut083
  Tool = -> Extrude050
FEATURE [Part::Cut] Cut085
  Base = -> Cut084
  Tool = -> Extrude168
FEATURE [Part::Extrusion] Extrude173
  Base = -> Circle030
  Dir = (0,0,1)
  DirMode = 2
  FaceMakerClass = Part::FaceMakerBullseye
  LengthFwd = 2
  LengthRev = 0
  Solid = false
  Symmetric = false
FEATURE [Part::Extrusion] Extrude174
  Base = -> Circle031
  Dir = (0,0,1)
  DirMode = 2
  FaceMakerClass = Part::FaceMakerBullseye
  LengthFwd = 2
  LengthRev = 0
  Solid = false
  Symmetric = false
FEATURE [Part::Cut] Cut086
  Base = -> Cut027
  Tool = -> Extrude174
FEATURE [Part::Cut] Cut087
  Base = -> Cut086
  Tool = -> Extrude173
FEATURE [Part::Cut] Cut088
  Base = -> Cut087
  Tool = -> Extrude160
FEATURE [Part::Cut] Cut089
  Base = -> Cut088
  Tool = -> Extrude088
FEATURE [Part::Cut] Cut090
  Base = -> Cut089
  Tool = -> Extrude086
FEATURE [Part::Part2DObjectPython] Wire  # Draft 2D object (typed FeaturePython)
  ChamferSize = 0
  Closed = true
  End = (0,0,0)
  FilletRadius = 0
  Length = 173.9
  MakeFace = true
  Placement = pos=(1.4e-14,-12.2,0) rot=(1,0,0;1.5708rad)
  Points = (8) [(0,0,0),(1.5,-4.59243e-17,0),(1.5,2.32995e-15,-10.7),(66.8,3.30717e-16,-10.7),(66.8,-1.98965e-15,-4.25),(68.3,-2.03557e-15,-4.25),+2 more]
  Start = (1.4e-14,-12.2,0)
  Subdivisions = 0
FEATURE [Part::Extrusion] Extrusion
  Base = -> Wire
  Dir = (0,0,0.5)
  DirMode = 0
  FaceMakerClass = Part::FaceMakerBullseye
  LengthFwd = 0
  LengthRev = 0
  Solid = true
  Symmetric = false
FEATURE [Part::Part2DObjectPython] Wire004  # Draft 2D object (typed FeaturePython)
  ChamferSize = 0
  Closed = true
  End = (0,-33.4,0)
  FilletRadius = 0
  Length = 167.7
  MakeFace = true
  Placement = pos=(1.4e-14,-24.5,0) rot=(0,0,1;0rad)
  Points = (8) [(0,0,0),(1.5,0,0),(1.5,-7.4,0),(66.8,-7.4,0),(66.8,-0.75,-8.88178e-16),(68.3,-0.75,-8.88178e-16),(68.3,-8.9,0),(-1.42613e-14,-8.9,0)]
  Start = (1.4e-14,-24.5,0)
  Subdivisions = 0
FEATURE [Part::Extrusion] Extrusion001
  Base = -> Wire004
  Dir = (0,0,0.5)
  DirMode = 0
  FaceMakerClass = Part::FaceMakerBullseye
  LengthFwd = 0
  LengthRev = 0
  Solid = true
  Symmetric = false
FEATURE [Part::Part2DObjectPython] Rectangle073  # Draft 2D object (typed FeaturePython)
  ChamferSize = 0
  Columns = 1
  FilletRadius = 0
  Height = 30.39
  Length = 65.29
  MakeFace = true
  Placement = pos=(2.03015,-165.606,0.5) rot=(0,0,1;0rad)
  Rows = 1
FEATURE [Part::MultiFuse] Fusion037  label="Fusion - PI Capsule"
  Shapes = -> [Cut085,Extrusion,Extrusion001]
FEATURE [Part::Part2DObjectPython] Circle041  # Draft 2D object (typed FeaturePython)
  FirstAngle = 0
  LastAngle = 0
  MakeFace = true
  Placement = pos=(5.67515,-138.911,0.5) rot=(0,0,1;0rad)
  Radius = 1.4
FEATURE [Part::Part2DObjectPython] Circle042  # Draft 2D object (typed FeaturePython)
  FirstAngle = 0
  LastAngle = 0
  MakeFace = true
  Placement = pos=(5.67515,-161.911,0.5) rot=(0,0,1;0rad)
  Radius = 1.4
FEATURE [Part::Part2DObjectPython] Circle043  # Draft 2D object (typed FeaturePython)
  FirstAngle = 0
  LastAngle = 0
  MakeFace = true
  Placement = pos=(63.6752,-138.911,0.5) rot=(0,0,1;0rad)
  Radius = 1.4
FEATURE [Part::Part2DObjectPython] Circle044  # Draft 2D object (typed FeaturePython)
  FirstAngle = 0
  LastAngle = 0
  MakeFace = true
  Placement = pos=(63.6752,-161.911,0.5) rot=(0,0,1;0rad)
  Radius = 1.4
FEATURE [Part::Extrusion] Extrude175
  Base = -> Rectangle073
  Dir = (0,0,1)
  DirMode = 2
  FaceMakerClass = Part::FaceMakerBullseye
  LengthFwd = 1.5
  LengthRev = 0
  Solid = false
  Symmetric = false
FEATURE [Part::Extrusion] Extrude176
  Base = -> Circle041
  Dir = (0,0,1)
  DirMode = 2
  FaceMakerClass = Part::FaceMakerBullseye
  LengthFwd = 1.5
  LengthRev = 0
  Solid = false
  Symmetric = false
FEATURE [Part::Extrusion] Extrude177
  Base = -> Circle042
  Dir = (0,0,1)
  DirMode = 2
  FaceMakerClass = Part::FaceMakerBullseye
  LengthFwd = 1.5
  LengthRev = 0
  Solid = false
  Symmetric = false
FEATURE [Part::Extrusion] Extrude178
  Base = -> Circle043
  Dir = (0,0,1)
  DirMode = 2
  FaceMakerClass = Part::FaceMakerBullseye
  LengthFwd = 1.5
  LengthRev = 0
  Solid = false
  Symmetric = false
FEATURE [Part::Extrusion] Extrude179
  Base = -> Circle044
  Dir = (0,0,1)
  DirMode = 2
  FaceMakerClass = Part::FaceMakerBullseye
  LengthFwd = 1.5
  LengthRev = 0
  Solid = false
  Symmetric = false
FEATURE [Part::Cut] Cut092
  Base = -> Extrude175
  Tool = -> Extrude178
FEATURE [Part::Cut] Cut093
  Base = -> Cut092
  Tool = -> Extrude179
FEATURE [Part::Cut] Cut094
  Base = -> Cut093
  Tool = -> Extrude176
FEATURE [Part::Cut] Cut095
  Base = -> Cut094
  Tool = -> Extrude177
FEATURE [Part::Part2DObjectPython] Wire005  # Draft 2D object (typed FeaturePython)
  ChamferSize = 0
  Closed = true
  End = (2.03015,-154.285,-27.4054)
  FilletRadius = 0
  Length = 48.5306
  MakeFace = true
  Placement = pos=(2.03015,-153.908,-26.421) rot=(0.663461,0.567609,0.487483;2.4534rad)
  Points = (30) [(0,0,0),(3.65235,10.85,-4.18846),(3.84601,11.3521,-4.38251),(4.20407,11.8325,-4.56959),(4.68334,12.2095,-4.71808),(5.2511,12.4577,-4.8179),+24 more]
  Start = (2.03015,-153.908,-26.421)
  Subdivisions = 0
FEATURE [Part::Part2DObjectPython] Circle001  # Draft 2D object (typed FeaturePython)
  FirstAngle = 0
  LastAngle = 0
  MakeFace = true
  Placement = pos=(2.03015,-150.411,-19.6751) rot=(0.57735,0.57735,-0.57735;4.18879rad)
  Radius = 1
FEATURE [Part::Part2DObjectPython] Circle002  # Draft 2D object (typed FeaturePython)
  FirstAngle = 0
  LastAngle = 0
  MakeFace = true
  Placement = pos=(2.03015,-150.403,-15.6959) rot=(0.57735,0.57735,-0.57735;4.18879rad)
  Radius = 1.00167
  Support = -> [Circle001]
FEATURE [Part::Part2DObjectPython] Circle046  # Draft 2D object (typed FeaturePython)
  FirstAngle = 0
  LastAngle = 0
  MakeFace = true
  Placement = pos=(2.03015,-150.428,-28.5) rot=(0.57735,0.57735,-0.57735;4.18879rad)
  Radius = 1.2
FEATURE [Part::Part2DObjectPython] Circle047  # Draft 2D object (typed FeaturePython)
  FirstAngle = 0
  LastAngle = 0
  MakeFace = true
  Placement = pos=(2.03015,-150.428,-29.4) rot=(0.57735,-0.57735,-0.57735;2.0944rad)
  Radius = 3.5
  Support = -> [Wire005]
FEATURE [Part::Part2DObjectPython] Circle048  # Draft 2D object (typed FeaturePython)
  FirstAngle = 0
  LastAngle = 0
  MakeFace = true
  Placement = pos=(2.03015,-150.428,-28.5) rot=(0.57735,-0.57735,-0.57735;2.0944rad)
  Radius = 5.99723
FEATURE [Part::Extrusion] Extrude180
  Base = -> Circle046
  Dir = (-1,-3e-16,-1e-16)
  DirMode = 2
  FaceMakerClass = Part::FaceMakerBullseye
  LengthFwd = 7
  LengthRev = 0
  Placement = pos=(5.5,-0.000154092,-0.9) rot=(0,0,1;0rad)
  Solid = false
  Symmetric = false
FEATURE [Part::Extrusion] Extrude182
  Base = -> Circle001
  Dir = (-1,-1e-16,-1e-16)
  DirMode = 2
  FaceMakerClass = Part::FaceMakerBullseye
  LengthFwd = 7
  LengthRev = 0
  Placement = pos=(5.5,-0.0154632,-2.23317) rot=(0,0,1;0rad)
  Solid = false
  Symmetric = false
FEATURE [Part::Extrusion] Extrude183
  Base = -> Circle002
  Dir = (-1,-1e-16,-1e-16)
  DirMode = 2
  FaceMakerClass = Part::FaceMakerBullseye
  LengthFwd = 7
  LengthRev = 0
  Placement = pos=(5.5,-0.0224193,0.595928) rot=(0,0,1;0rad)
  Solid = false
  Symmetric = false
FEATURE [Part::Part2DObjectPython] Circle049  # Draft 2D object (typed FeaturePython)
  FirstAngle = 0
  LastAngle = 0
  MakeFace = true
  Placement = pos=(2.03015,-150.425,-15.1) rot=(0.57735,-0.57735,-0.57735;2.0944rad)
  Radius = 2
FEATURE [Part::Extrusion] Extrude185
  Base = -> Circle049
  Dir = (-1,0,0)
  DirMode = 2
  FaceMakerClass = Part::FaceMakerBullseye
  LengthFwd = 1.5
  LengthRev = 0
  Solid = false
  Symmetric = false
FEATURE [Part::Part2DObjectPython] Wire007  # Draft 2D object (typed FeaturePython)
  ChamferSize = 0
  Closed = true
  End = (2.03015,-156.088,-30.4801)
  FilletRadius = 0
  Length = 106.482
  MakeFace = true
  Placement = pos=(2.03015,-165.606,0.5) rot=(0.57735,-0.57735,-0.57735;2.0944rad)
  Points = (4) [(0,0,0),(-30.39,7.77156e-16,8.88178e-16),(-20.8392,-30.9198,-5.91506e-08),(-9.5171,-30.9801,-5.91506e-08)]
  Start = (2.03015,-165.606,0.5)
  Subdivisions = 0
FEATURE [Part::Extrusion] Extrude186
  Base = -> Wire007
  Dir = (-1,0,0)
  DirMode = 2
  FaceMakerClass = Part::FaceMakerBullseye
  LengthFwd = -1.5
  LengthRev = 0
  Solid = false
  Symmetric = false
FEATURE [Part::Extrusion] Extrude187
  Base = -> Circle048
  Dir = (-1,0,0)
  DirMode = 2
  FaceMakerClass = Part::FaceMakerBullseye
  LengthFwd = -1.5
  LengthRev = 0
  Solid = false
  Symmetric = false
FEATURE [Part::Part2DObjectPython] Circle050  # Draft 2D object (typed FeaturePython)
  FirstAngle = 0
  LastAngle = 0
  MakeFace = true
  Placement = pos=(2.03015,-150.428,-28.5) rot=(0.57735,-0.57735,-0.57735;2.0944rad)
  Radius = 5.99723
FEATURE [Part::Part2DObjectPython] Circle051  # Draft 2D object (typed FeaturePython)
  FirstAngle = 0
  LastAngle = 0
  MakeFace = true
  Placement = pos=(2.03015,-150.423,-14.2392) rot=(0.57735,-0.57735,-0.57735;2.0944rad)
  Radius = 4.4
FEATURE [Part::Extrusion] Extrude189
  Base = -> Circle051
  Dir = (-1,0,0)
  DirMode = 2
  FaceMakerClass = Part::FaceMakerBullseye
  LengthFwd = 1.5
  LengthRev = 0
  Placement = pos=(2.38051e-08,-0.00802178,-1.05515) rot=(0,0,1;0rad)
  Solid = false
  Symmetric = false
FEATURE [Part::Extrusion] Extrude190
  Base = -> Circle050
  Dir = (-1,0,0)
  DirMode = 2
  FaceMakerClass = Part::FaceMakerBullseye
  LengthFwd = 1.5
  LengthRev = 0
  Placement = pos=(0,-0.000154092,-0.9) rot=(0,0,1;0rad)
  Solid = false
  Symmetric = false
FEATURE [Part::Part2DObjectPython] Wire010  # Draft 2D object (typed FeaturePython)
  ChamferSize = 0
  Closed = true
  End = (2.03015,-135.216,0.5)
  FilletRadius = 0
  Length = 106.482
  MakeFace = true
  Placement = pos=(2.03015,-165.606,0.5) rot=(1,0,0;3.14159rad)
  Points = (4) [(0,0,0),(5.91506e-08,-9.5171,30.9801),(5.91506e-08,-20.8392,30.9198),(-7.99361e-15,-30.39,0)]
  Start = (2.03015,-165.606,0.5)
  Subdivisions = 0
FEATURE [Part::Part2DObjectPython] Circle052  # Draft 2D object (typed FeaturePython)
  FirstAngle = 0
  LastAngle = 0
  MakeFace = true
  Placement = pos=(2.03015,-150.428,-28.5) rot=(0.57735,-0.57735,-0.57735;2.0944rad)
  Radius = 5.99723
FEATURE [Part::MultiFuse] Fusion040
  Placement = pos=(63.79,0,-1e-16) rot=(0,0,1;0rad)
  Shapes = -> [Extrude186,Extrude187]
FEATURE [Part::Extrusion] Extrude191
  Base = -> Circle052
  Dir = (-1,0,0)
  DirMode = 2
  FaceMakerClass = Part::FaceMakerBullseye
  LengthFwd = -1.5
  LengthRev = 0
  Solid = false
  Symmetric = false
FEATURE [Part::Extrusion] Extrude192
  Base = -> Wire010
  Dir = (65.29,0,-1e-16)
  DirLink = -> Cut095 [Edge3]
  DirMode = 1
  FaceMakerClass = Part::FaceMakerBullseye
  LengthFwd = 1.5
  LengthRev = 0
  Solid = false
  Symmetric = false
FEATURE [Part::MultiFuse] Fusion041
  Shapes = -> [Extrude191,Extrude192]
FEATURE [Part::Part2DObjectPython] Line  # Draft 2D object (typed FeaturePython)
  ChamferSize = 0
  Closed = false
  End = (53.5252,-150.427,-28.5)
  FilletRadius = 0
  Length = 37.7
  MakeFace = true
  Placement = pos=(15.8252,-150.425,-28.5) rot=(0.57735,-0.57735,-0.57735;2.0944rad)
  Points = (2) [(0,0,0),(0.00173367,0,-37.7)]
  Start = (15.8252,-150.425,-28.5)
  Subdivisions = 0
FEATURE [Part::Part2DObjectPython] Line001  # Draft 2D object (typed FeaturePython)
  ChamferSize = 0
  Closed = false
  End = (2.03015,-114.603,12.9692)
  FilletRadius = 0
  Length = 2.4
  MakeFace = true
  Placement = pos=(2.03015,-112.203,12.9692) rot=(0.57735,-0.57735,-0.57735;2.0944rad)
  Points = (2) [(0,0,0),(2.4,0,0)]
  Start = (2.03015,-112.203,12.9692)
  Subdivisions = 0
FEATURE [Part::Part2DObjectPython] Circle054  # Draft 2D object (typed FeaturePython)
  FirstAngle = 0
  LastAngle = 0
  MakeFace = true
  Placement = pos=(2.03015,-150.425,-28.5) rot=(0.57735,-0.57735,-0.57735;2.0944rad)
  Radius = 0.5
FEATURE [Part::Extrusion] Extrude193
  Base = -> Circle054
  Dir = (-1,0,0)
  DirMode = 2
  FaceMakerClass = Part::FaceMakerBullseye
  LengthFwd = -10
  LengthRev = 0
  Solid = false
  Symmetric = false
FEATURE [Part::Part2DObjectPython] Wire011  # Draft 2D object (typed FeaturePython)
  ChamferSize = 0
  Closed = true
  End = (55.3508,-150.41,0.5)
  FilletRadius = 0
  Length = 7.8541
  MakeFace = true
  Placement = pos=(56.8508,-150.41,0.5) rot=(0.57735,0.57735,0.57735;2.0944rad)
  Points = (3) [(0,0,0),(0,-3,-1.5),(0,0,-1.5)]
  Start = (56.8508,-150.41,0.5)
  Subdivisions = 0
FEATURE [Part::Extrusion] Extrude194
  Base = -> Wire011
  Dir = (0,-30.39,-8e-16)
  DirMode = 1
  FaceMakerClass = Part::FaceMakerBullseye
  LengthFwd = 0
  LengthRev = 0
  Placement = pos=(0,15.1945,4e-16) rot=(0,0,1;0rad)
  Solid = false
  Symmetric = false
FEATURE [Part::Part2DObjectPython] Wire012  # Draft 2D object (typed FeaturePython)
  ChamferSize = 0
  Closed = true
  End = (55.3508,-136.141,-2.5)
  FilletRadius = 0
  Length = 7.06533
  MakeFace = true
  Placement = pos=(55.3508,-135.216,0.5) rot=(0.57735,0.57735,0.57735;2.0944rad)
  Points = (3) [(0,0,0),(0,-3,0),(-0.925744,-3,-3.40393e-07)]
  Start = (55.3508,-135.216,0.5)
  Subdivisions = 0
  Support = -> [Extrude194]
FEATURE [Part::Extrusion] Extrude195
  Base = -> Wire012
  Dir = (1,0,0)
  DirMode = 2
  FaceMakerClass = Part::FaceMakerBullseye
  LengthFwd = 10
  LengthRev = 0
  Solid = false
  Symmetric = false
FEATURE [Part::Cut] Cut099
  Base = -> Extrude194
  Tool = -> Extrude195
FEATURE [Part::Part2DObjectPython] Wire013  # Draft 2D object (typed FeaturePython)
  ChamferSize = 0
  Closed = true
  End = (55.3507,-164.683,-2.49998)
  FilletRadius = 0
  Length = 7.06064
  MakeFace = true
  Placement = pos=(55.3508,-165.606,-2.5) rot=(0.57735,0.57735,0.57735;2.0944rad)
  Points = (3) [(0,0,0),(0,3,0),(0.922141,2.43187e-05,-6.13755e-05)]
  Start = (55.3508,-165.606,-2.5)
  Subdivisions = 0
FEATURE [Part::Extrusion] Extrude196
  Base = -> Wire013
  Dir = (1,0,0)
  DirMode = 2
  FaceMakerClass = Part::FaceMakerBullseye
  LengthFwd = 10
  LengthRev = 0
  Solid = false
  Symmetric = false
FEATURE [Part::Part2DObjectPython] Wire014  # Draft 2D object (typed FeaturePython)
  ChamferSize = 0
  Closed = true
  End = (55.3507,-164.683,-2.49998)
  FilletRadius = 0
  Length = 7.06064
  MakeFace = true
  Placement = pos=(55.3508,-165.606,-2.5) rot=(0.57735,0.57735,0.57735;2.0944rad)
  Points = (3) [(0,0,0),(0,3,0),(0.922141,2.43187e-05,-6.13755e-05)]
  Start = (55.3508,-165.606,-2.5)
  Subdivisions = 0
FEATURE [Part::Extrusion] Extrude198
  Base = -> Wire014
  Dir = (1,0,0)
  DirMode = 2
  FaceMakerClass = Part::FaceMakerBullseye
  LengthFwd = 10
  LengthRev = 0
  Solid = false
  Symmetric = false
FEATURE [Part::Part2DObjectPython] Wire015  # Draft 2D object (typed FeaturePython)
  ChamferSize = 0
  Closed = true
  End = (55.3508,-150.41,0.5)
  FilletRadius = 0
  Length = 7.8541
  MakeFace = true
  Placement = pos=(56.8508,-150.41,0.5) rot=(0.57735,0.57735,0.57735;2.0944rad)
  Points = (3) [(0,0,0),(0,-3,-1.5),(0,0,-1.5)]
  Start = (56.8508,-150.41,0.5)
  Subdivisions = 0
FEATURE [Part::Extrusion] Extrude197
  Base = -> Wire015
  Dir = (0,-30.39,-8e-16)
  DirMode = 1
  FaceMakerClass = Part::FaceMakerBullseye
  LengthFwd = 0
  LengthRev = 0
  Placement = pos=(0,15.1945,0) rot=(0,0,1;0rad)
  Solid = false
  Symmetric = false
FEATURE [Part::Part2DObjectPython] Wire016  # Draft 2D object (typed FeaturePython)
  ChamferSize = 0
  Closed = true
  End = (55.3508,-136.141,-2.5)
  FilletRadius = 0
  Length = 7.06533
  MakeFace = true
  Placement = pos=(55.3508,-135.216,0.5) rot=(0.57735,0.57735,0.57735;2.0944rad)
  Points = (3) [(0,0,0),(0,-3,0),(-0.925744,-3,-3.40393e-07)]
  Start = (55.3508,-135.216,0.5)
  Subdivisions = 0
  Support = -> [Extrude197]
FEATURE [Part::Extrusion] Extrude199
  Base = -> Wire016
  Dir = (1,0,0)
  DirMode = 2
  FaceMakerClass = Part::FaceMakerBullseye
  LengthFwd = 10
  LengthRev = 0
  Solid = false
  Symmetric = false
FEATURE [Part::Cut] Cut102
  Base = -> Extrude197
  Tool = -> Extrude199
FEATURE [Part::Cut] Cut101
  Base = -> Cut102
  Placement = pos=(-40.6256,0.00225998,1.38e-14) rot=(0,0,1;0rad)
  Tool = -> Extrude198
FEATURE [Part::Part2DObjectPython] Wire017  # Draft 2D object (typed FeaturePython)
  ChamferSize = 0
  Closed = true
  End = (55.3507,-164.683,-2.49998)
  FilletRadius = 0
  Length = 7.06064
  MakeFace = true
  Placement = pos=(55.3508,-165.606,-2.5) rot=(0.57735,0.57735,0.57735;2.0944rad)
  Points = (3) [(0,0,0),(0,3,0),(0.922141,2.43187e-05,-6.13755e-05)]
  Start = (55.3508,-165.606,-2.5)
  Subdivisions = 0
FEATURE [Part::Extrusion] Extrude201
  Base = -> Wire017
  Dir = (1,0,0)
  DirMode = 2
  FaceMakerClass = Part::FaceMakerBullseye
  LengthFwd = 10
  LengthRev = 0
  Solid = false
  Symmetric = false
FEATURE [Part::Part2DObjectPython] Wire018  # Draft 2D object (typed FeaturePython)
  ChamferSize = 0
  Closed = true
  End = (55.3508,-150.41,0.5)
  FilletRadius = 0
  Length = 7.8541
  MakeFace = true
  Placement = pos=(56.8508,-150.41,0.5) rot=(0.57735,0.57735,0.57735;2.0944rad)
  Points = (3) [(0,0,0),(0,-3,-1.5),(0,0,-1.5)]
  Start = (56.8508,-150.41,0.5)
  Subdivisions = 0
FEATURE [Part::Extrusion] Extrude200
  Base = -> Wire018
  Dir = (0,-30.39,-8e-16)
  DirMode = 1
  FaceMakerClass = Part::FaceMakerBullseye
  LengthFwd = 0
  LengthRev = 0
  Placement = pos=(0,15.1945,0) rot=(0,0,1;0rad)
  Solid = false
  Symmetric = false
FEATURE [Part::Part2DObjectPython] Wire019  # Draft 2D object (typed FeaturePython)
  ChamferSize = 0
  Closed = true
  End = (55.3508,-136.141,-2.5)
  FilletRadius = 0
  Length = 7.06533
  MakeFace = true
  Placement = pos=(55.3508,-135.216,0.5) rot=(0.57735,0.57735,0.57735;2.0944rad)
  Points = (3) [(0,0,0),(0,-3,0),(-0.925744,-3,-3.40393e-07)]
  Start = (55.3508,-135.216,0.5)
  Subdivisions = 0
  Support = -> [Extrude200]
FEATURE [Part::Extrusion] Extrude202
  Base = -> Wire019
  Dir = (1,0,0)
  DirMode = 2
  FaceMakerClass = Part::FaceMakerBullseye
  LengthFwd = 10
  LengthRev = 0
  Solid = false
  Symmetric = false
FEATURE [Part::Cut] Cut104
  Base = -> Extrude200
  Tool = -> Extrude202
FEATURE [Part::Cut] Cut103
  Base = -> Cut104
  Placement = pos=(107.776,-300.821,-7.8e-15) rot=(0,0,1;3.14159rad)
  Tool = -> Extrude201
FEATURE [Part::Part2DObjectPython] Wire021  # Draft 2D object (typed FeaturePython)
  ChamferSize = 0
  Closed = true
  End = (55.3508,-150.41,0.5)
  FilletRadius = 0
  Length = 7.8541
  MakeFace = true
  Placement = pos=(56.8508,-150.41,0.5) rot=(0.57735,0.57735,0.57735;2.0944rad)
  Points = (3) [(0,0,0),(0,-3,-1.5),(0,0,-1.5)]
  Start = (56.8508,-150.41,0.5)
  Subdivisions = 0
FEATURE [Part::Part2DObjectPython] Wire022  # Draft 2D object (typed FeaturePython)
  ChamferSize = 0
  Closed = true
  End = (55.3507,-164.683,-2.49998)
  FilletRadius = 0
  Length = 7.06064
  MakeFace = true
  Placement = pos=(55.3508,-165.606,-2.5) rot=(0.57735,0.57735,0.57735;2.0944rad)
  Points = (3) [(0,0,0),(0,3,0),(0.922141,2.43187e-05,-6.13755e-05)]
  Start = (55.3508,-165.606,-2.5)
  Subdivisions = 0
FEATURE [Part::Extrusion] Extrude204
  Base = -> Wire022
  Dir = (1,0,0)
  DirMode = 2
  FaceMakerClass = Part::FaceMakerBullseye
  LengthFwd = 10
  LengthRev = 0
  Solid = false
  Symmetric = false
FEATURE [Part::Extrusion] Extrude205
  Base = -> Wire021
  Dir = (0,-30.39,-8e-16)
  DirMode = 1
  FaceMakerClass = Part::FaceMakerBullseye
  LengthFwd = 0
  LengthRev = 0
  Placement = pos=(0,15.1945,0) rot=(0,0,1;0rad)
  Solid = false
  Symmetric = false
FEATURE [Part::Part2DObjectPython] Wire020  # Draft 2D object (typed FeaturePython)
  ChamferSize = 0
  Closed = true
  End = (55.3508,-136.141,-2.5)
  FilletRadius = 0
  Length = 7.06533
  MakeFace = true
  Placement = pos=(55.3508,-135.216,0.5) rot=(0.57735,0.57735,0.57735;2.0944rad)
  Points = (3) [(0,0,0),(0,-3,0),(-0.925744,-3,-3.40393e-07)]
  Start = (55.3508,-135.216,0.5)
  Subdivisions = 0
  Support = -> [Extrude205]
FEATURE [Part::Extrusion] Extrude203
  Base = -> Wire020
  Dir = (1,0,0)
  DirMode = 2
  FaceMakerClass = Part::FaceMakerBullseye
  LengthFwd = 10
  LengthRev = 0
  Solid = false
  Symmetric = false
FEATURE [Part::Cut] Cut105
  Base = -> Extrude205
  Tool = -> Extrude203
FEATURE [Part::Cut] Cut106
  Base = -> Cut105
  Placement = pos=(68.5759,-300.819,6e-15) rot=(0,0,1;3.14159rad)
  Tool = -> Extrude204
FEATURE [Part::Extrusion] Extrude206
  Base = -> Circle034
  Dir = (0,0,1)
  DirMode = 2
  FaceMakerClass = Part::FaceMakerBullseye
  LengthFwd = -2
  LengthRev = 0
  Solid = false
  Symmetric = false
FEATURE [Part::Cut] Cut107
  Base = -> Cut090
  Tool = -> Extrude206
FEATURE [Part::MultiFuse] Fusion047  label="Fusion - Lens Cover"
  Shapes = -> [Extrude095,Cut107]
FEATURE [Part::Cut] Cut060
  Base = -> Cut046
  Tool = -> Extrude140
FEATURE [Part::Cut] Cut061
  Base = -> Cut060
  Tool = -> Extrude141
FEATURE [Part::Cut] Cut062
  Base = -> Cut061
  Tool = -> Extrude128
FEATURE [Part::Cut] Cut063
  Base = -> Cut062
  Tool = -> Extrude117
FEATURE [Part::Cut] Cut074
  Base = -> Cut063
  Tool = -> Extrude162
FEATURE [Part::Part2DObjectPython] Circle040  # Draft 2D object (typed FeaturePython)
  FirstAngle = 0
  LastAngle = 0
  MakeFace = true
  Placement = pos=(80.1343,-74.566,-3.6) rot=(1,0,0;3.14159rad)
  Radius = 0.65
  Support = -> [Cut074]
FEATURE [Part::Extrusion] Extrude167
  Base = -> Circle040
  Dir = (0,0,-1)
  DirMode = 2
  FaceMakerClass = Part::FaceMakerBullseye
  LengthFwd = -10
  LengthRev = 0
  Solid = false
  Symmetric = false
FEATURE [Part::MultiFuse] Fusion033
  Shapes = -> [Fusion025,Fusion026,Fusion032,Fusion024,Cut074]
FEATURE [Part::Cut] Cut075
  Base = -> Fusion033
  Tool = -> Extrude167
FEATURE [Part::Cut] Cut076
  Base = -> Cut075
  Tool = -> Extrude165
FEATURE [Part::Cut] Cut077
  Base = -> Cut076
  Tool = -> Extrude163
FEATURE [Part::Cut] Cut078  label="Cut - Lens Capsule"
  Base = -> Cut077
  Placement = pos=(101.469,0,-19.6) rot=(0,1,0;3.14159rad)
  Tool = -> Extrude166
FEATURE [Part::Part2DObjectPython] Rectangle072  # Draft 2D object (typed FeaturePython)
  ChamferSize = 0
  Columns = 1
  FilletRadius = 0
  Height = 33.4
  Length = 32.9
  MakeFace = true
  Placement = pos=(17.8343,-47.366,-18.8) rot=(1,0,0;3.14159rad)
  Rows = 1
  Support = -> [Cut078]
FEATURE [Part::Extrusion] Extrude172
  Base = -> Rectangle072
  Dir = (1e-16,0,-1)
  DirMode = 2
  FaceMakerClass = Part::FaceMakerBullseye
  LengthFwd = 0.5
  LengthRev = 0
  Solid = false
  Symmetric = false
FEATURE [Part::MultiFuse] Fusion035  label="Fusion - Lens Capsule"
  Shapes = -> [Cut078,Extrude172]
FEATURE [Part::Part2DObjectPython] Rectangle077  # Draft 2D object (typed FeaturePython)
  ChamferSize = 0
  Columns = 1
  FilletRadius = 0
  Height = 33.4
  Length = 0.2
  MakeFace = true
  Placement = pos=(50.5343,-80.766,-19.3) rot=(0,0,1;0rad)
  Rows = 1
FEATURE [Part::Extrusion] Extrude207
  Base = -> Rectangle077
  Dir = (0,0,1)
  DirMode = 2
  FaceMakerClass = Part::FaceMakerBullseye
  LengthFwd = 1.5
  LengthRev = 0
  Solid = false
  Symmetric = false
FEATURE [Part::Cut] Cut108  label="Cut-Lens Capsule"
  Base = -> Fusion035
  Tool = -> Extrude207
FEATURE [Part::Cut] Cut100
  Base = -> Cut099
  Placement = pos=(-1.42562,0.00052631,1e-16) rot=(0,0,1;0rad)
  Tool = -> Extrude196
FEATURE [Part::Part2DObjectPython] Wire023  # Draft 2D object (typed FeaturePython)
  ChamferSize = 0
  Closed = true
  End = (2.03015,-152.425,-15.1)
  FilletRadius = 0
  Length = 39.7569
  MakeFace = true
  Placement = pos=(2.03015,-148.425,-15.1) rot=(0.57735,-0.57735,-0.57735;2.0944rad)
  Points = (4) [(0,0,0),(-1.49755,-14.3,0),(5.50245,-14.3,-4.44089e-16),(4,0,0)]
  Start = (2.03015,-148.425,-15.1)
  Subdivisions = 0
FEATURE [Part::Extrusion] Extrude208
  Base = -> Wire023
  Dir = (-1,0,0)
  DirMode = 2
  FaceMakerClass = Part::FaceMakerBullseye
  LengthFwd = 1.5
  LengthRev = 0
  Solid = false
  Symmetric = false
FEATURE [Part::Extrusion] Extrude209
  Base = -> Circle047
  Dir = (-1,0,0)
  DirMode = 2
  FaceMakerClass = Part::FaceMakerBullseye
  LengthFwd = 1.5
  LengthRev = 0
  Solid = false
  Symmetric = false
FEATURE [Part::MultiFuse] Fusion048
  Shapes = -> [Extrude209,Extrude208,Extrude185]
FEATURE [Part::FeaturePython] BooleanFragments  # WARN: FeaturePython — macro-defined, semantics opaque (R4)
  Mode = 0
  Objects = -> [Fusion048,Extrude180,Extrude182,Extrude183]
  Placement = pos=(63.79,0.000154092,0.9) rot=(0,0,1;0rad)
  Tolerance = 0
FEATURE [Part::Part2DObjectPython] Wire024  # Draft 2D object (typed FeaturePython)
  ChamferSize = 0
  Closed = true
  End = (2.03015,-146.031,-15.2944)
  FilletRadius = 0
  Length = 47.0337
  MakeFace = true
  Placement = pos=(2.03015,-154.831,-15.2944) rot=(0.57735,0.57735,0.57735;2.0944rad)
  Points = (4) [(0,0,0),(-1.51456,-13.1499,7.56886e-09),(10.3051,-13.0908,7.56886e-09),(8.8,0,-4.44089e-16)]
  Start = (2.03015,-154.831,-15.2944)
  Subdivisions = 0
FEATURE [Part::Extrusion] Extrude210
  Base = -> Wire024
  Dir = (1,0,0)
  DirMode = 2
  FaceMakerClass = Part::FaceMakerBullseye
  LengthFwd = -1.5
  LengthRev = 0
  Solid = false
  Symmetric = false
FEATURE [Part::MultiFuse] Fusion049
  Placement = pos=(63.79,0.000154092,0.9) rot=(0,0,1;0rad)
  Shapes = -> [Extrude189,Extrude210,Extrude190]
FEATURE [Part::MultiFuse] Fusion050
  Shapes = -> [Fusion049,Fusion040]
FEATURE [Part::Cut] Cut109
  Base = -> Fusion050
  Placement = pos=(-13.395,0.00052631,0) rot=(0,0,1;0rad)
  Tool = -> BooleanFragments
FEATURE [Part::Part2DObjectPython] Line006  # Draft 2D object (typed FeaturePython)
  ChamferSize = 0
  Closed = false
  End = (53.5252,-149.227,-28.5)
  FilletRadius = 0
  Length = 2.4
  MakeFace = true
  Placement = pos=(53.5252,-151.627,-28.5) rot=(1,0,0;1.5708rad)
  Points = (2) [(0,0,0),(0,0,-2.4)]
  Start = (53.5252,-151.627,-28.5)
  Subdivisions = 0
FEATURE [Part::Part2DObjectPython] Line003  # Draft 2D object (typed FeaturePython)
  ChamferSize = 0
  Closed = false
  End = (2.03015,-150.411,0.5)
  FilletRadius = 0
  Length = 65.29
  MakeFace = true
  Placement = pos=(67.3202,-150.411,0.5) rot=(0.57735,0.57735,0.57735;2.0944rad)
  Points = (2) [(0,0,0),(0,1.11022e-16,-65.29)]
  Start = (67.3202,-150.411,0.5)
  Subdivisions = 0
FEATURE [Part::Part2DObjectPython] Rectangle079  # Draft 2D object (typed FeaturePython)
  ChamferSize = 0
  Columns = 1
  FilletRadius = 0
  Height = 29
  Length = 65.29
  MakeFace = true
  Placement = pos=(2.03015,-150.427,-28.5) rot=(1,0,0;1.5708rad)
  Rows = 1
FEATURE [Part::Part2DObjectPython] Circle056  # Draft 2D object (typed FeaturePython)
  FirstAngle = 0
  LastAngle = 0
  MakeFace = true
  Placement = pos=(3.53015,-182.781,-40.3997) rot=(0.57735,0.57735,0.57735;2.0944rad)
  Radius = 6
  Support = -> [Fusion041]
FEATURE [Part::Extrusion] Extrude211
  Base = -> Circle056
  Dir = (1,0,0)
  DirMode = 2
  FaceMakerClass = Part::FaceMakerBullseye
  LengthFwd = 15
  LengthRev = 0
  Solid = false
  Symmetric = false
FEATURE [Part::Sphere] Sphere
  Angle1 = -90
  Angle2 = 90
  Angle3 = 360
  AttacherType = Attacher::AttachEngine3D
  Placement = pos=(18.5302,-182.781,-40.3997) rot=(0,0,1;0rad)
  Radius = 8
FEATURE [Part::Sphere] Sphere001
  Angle1 = -90
  Angle2 = 90
  Angle3 = 360
  AttacherType = Attacher::AttachEngine3D
  Placement = pos=(0,-179.118,-7.52533) rot=(0,0,1;0rad)
  Radius = 2.95
FEATURE [Part::Cut] Cut110
  Base = -> Extrude211
  Tool = -> Sphere
FEATURE [Part::Part2DObjectPython] Rectangle080  # Draft 2D object (typed FeaturePython)
  ChamferSize = 0
  Columns = 1
  FilletRadius = 0
  Height = 18.2864
  Length = 24.2574
  MakeFace = true
  Placement = pos=(0,-191.247,-16.6685) rot=(0.57735,0.57735,0.57735;2.0944rad)
  Rows = 1
FEATURE [Part::FeaturePython] Slice  # WARN: FeaturePython — macro-defined, semantics opaque (R4)
  Base = -> Sphere001
  Mode = 1
  Tolerance = 0
  Tools = -> [Rectangle080]
FEATURE [Part::FeaturePython] Slice_child0  label="Slice.0"  # WARN: FeaturePython — macro-defined, semantics opaque (R4)
  Base = -> Slice
  FilterType = 1
  Invert = false
  OverrideMaxVal = 0
  Placement = pos=(10.2887,-3.66293,-32.8744) rot=(0,0,1;0rad)
  WindowFrom = 80
  WindowTo = 100
  items = 0
FEATURE [Part::FeaturePython] Slice_child1  label="Slice.1"  # WARN: FeaturePython — macro-defined, semantics opaque (R4)
  Base = -> Slice
  FilterType = 1
  Invert = false
  OverrideMaxVal = 0
  WindowFrom = 80
  WindowTo = 100
  items = 1
FEATURE [Part::Part2DObjectPython] Rectangle081  # Draft 2D object (typed FeaturePython)
  ChamferSize = 0
  Columns = 1
  FilletRadius = 0
  Height = 17.0653
  Length = 22.0369
  MakeFace = true
  Placement = pos=(11,-193.8,-48.9324) rot=(0.57735,0.57735,0.57735;2.0944rad)
  Rows = 1
FEATURE [Part::MultiFuse] Fusion051
  Shapes = -> [Cut110,Slice_child0]
FEATURE [App::DocumentObjectGroup] GrExplode_Slice  label="Exploded Slice"
  Group = -> [Slice_child1,Fusion051]
FEATURE [Part::FeaturePython] Slice001  # WARN: FeaturePython — macro-defined, semantics opaque (R4)
  Base = -> Fusion051
  Mode = 1
  Tolerance = 0
  Tools = -> [Rectangle081]
FEATURE [App::DocumentObjectGroup] GrExplode_Slice001  label="Exploded Slice001"
FEATURE [Part::FeaturePython] Slice001_child0  label="Slice001.0"  # WARN: FeaturePython — macro-defined, semantics opaque (R4)
  Base = -> Slice001
  FilterType = 1
  Invert = false
  OverrideMaxVal = 0
  Placement = pos=(-7.46985,32.3536,11.8997) rot=(0,0,1;0rad)
  WindowFrom = 80
  WindowTo = 100
  items = 0
FEATURE [Part::MultiFuse] Fusion052
  Shapes = -> [Fusion041,Slice001_child0]
FEATURE [Part::Cut] Cut111
  Base = -> Fusion052
  Placement = pos=(11.195,0.00225998,7.1e-15) rot=(0,0,1;0rad)
  Tool = -> Extrude193
FEATURE [Part::Part2DObjectPython] Line010  # Draft 2D object (typed FeaturePython)
  ChamferSize = 0
  Closed = false
  End = (15.8252,-156.425,-28.5)
  FilletRadius = 0
  Length = 12
  MakeFace = true
  Placement = pos=(15.8252,-144.425,-28.5) rot=(0.57735,0.57735,0.57735;2.0944rad)
  Points = (2) [(0,0,0),(-12,0,0)]
  Start = (15.8252,-144.425,-28.5)
  Subdivisions = 0
FEATURE [Part::Part2DObjectPython] Line011  # Draft 2D object (typed FeaturePython)
  ChamferSize = 0
  Closed = false
  End = (15.8252,-150.425,30.3048)
  FilletRadius = 0
  Length = 58.8048
  MakeFace = true
  Placement = pos=(15.8252,-150.425,-28.5) rot=(0.57735,0.57735,0.57735;2.0944rad)
  Points = (2) [(0,0,0),(0,58.8048,0)]
  Start = (15.8252,-150.425,-28.5)
  Subdivisions = 0
FEATURE [Part::Part2DObjectPython] Line013  # Draft 2D object (typed FeaturePython)
  ChamferSize = 0
  Closed = false
  End = (34.6752,-150.426,-28.5)
  FilletRadius = 0
  Length = 29
  MakeFace = true
  Placement = pos=(34.6752,-150.411,0.5) rot=(0.57735,0.57735,0.57735;2.0944rad)
  Points = (2) [(0,0,0),(-0.0156504,-29,-7.19697e-07)]
  Start = (34.6752,-150.411,0.5)
  Subdivisions = 0
FEATURE [Part::MultiFuse] Fusion053
  Placement = pos=(1.1,-5.05846e-05,0) rot=(0,0,1;0rad)
  Shapes = -> [Cut109,Cut111,Cut101,Cut100,Cut103,Cut106]
